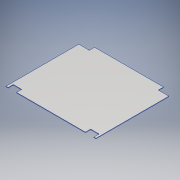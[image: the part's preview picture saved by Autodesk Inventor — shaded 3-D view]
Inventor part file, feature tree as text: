
AUTODESK INVENTOR PART (.ipt)
format: ipt  version: 2017 (Build 210142000, 142)  size: 126,976 bytes
history: native  units: mm
features: extrude x1, sketch x1
ambient origin geometry x8: Origin, YZ Plane, XZ Plane, XY Plane, X Axis, Y Axis, Z Axis, Center Point
bodies: Solid1 (feature_tree)
feature tree (2):
  extrude  "Extrusion1"  Depth=3.175mm TaperAngle=0.0deg
  sketch  "Sketch1"  dims[d14=414.02mm d17=3.175mm d18=0.0mm d20=60.325mm d22=28.105mm d23=60.325mm d28=44.45mm d29=50.8mm d34=437.68mm d38=437.68mm]
